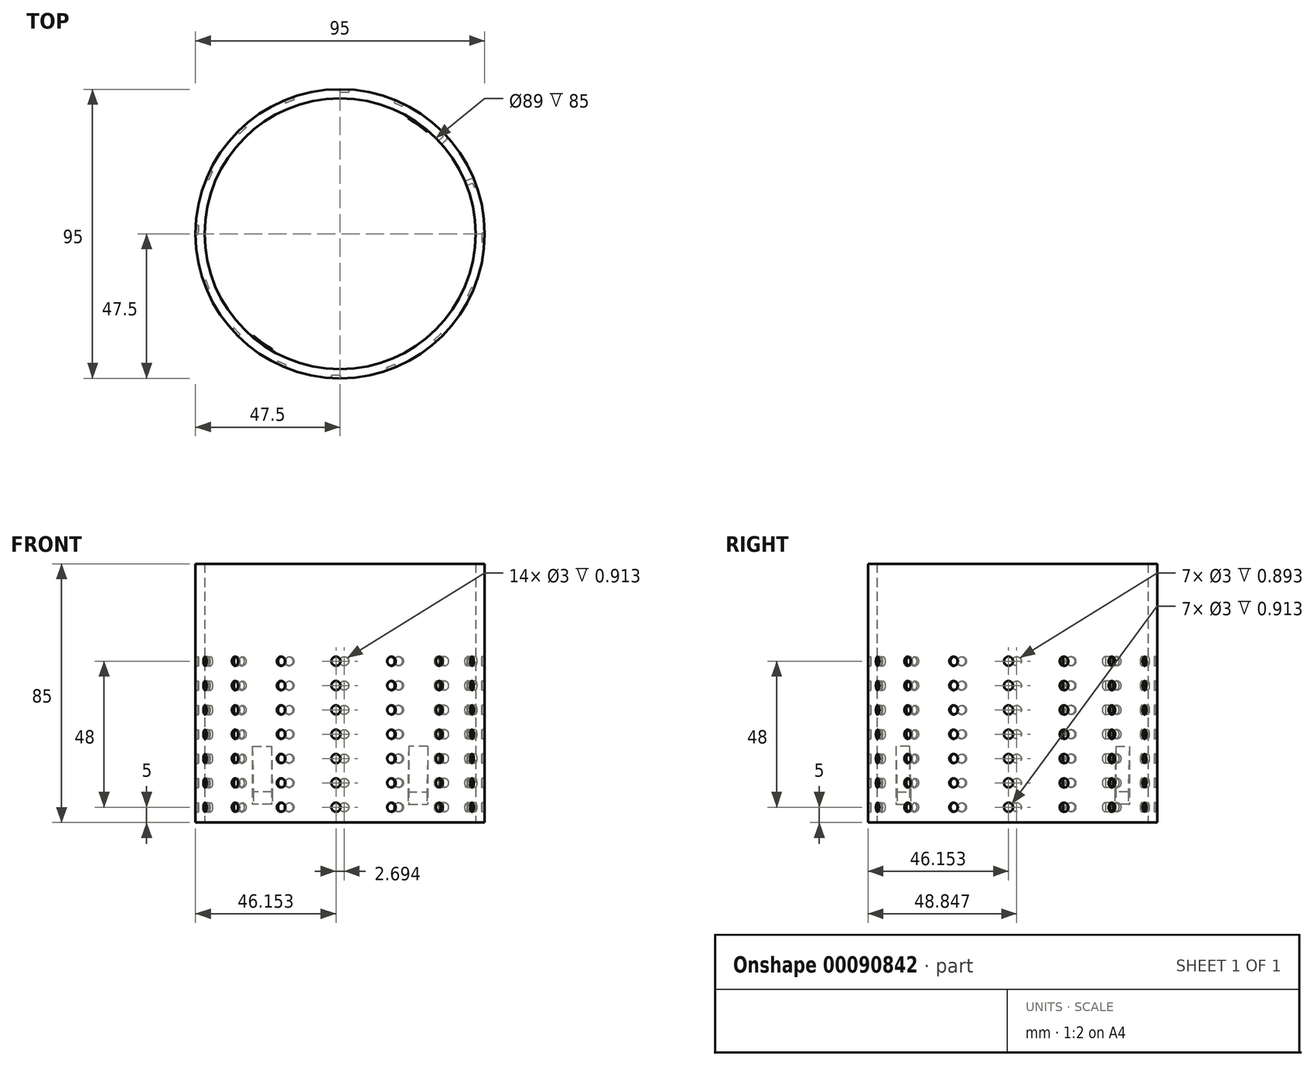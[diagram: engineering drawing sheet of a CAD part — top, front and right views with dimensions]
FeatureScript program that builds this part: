
annotation { "Feature Type Name" : "Feature", "Feature Type Description" : "" }
export const myFeature = defineFeature(function(context is Context, id is Id, definition is map)
    precondition{}
    {
        {
            var Q0;
            Q0=qCreatedBy(makeId("Top.planeOp"),FACE);
            var sketch = newSketch(context, id + "F0", { "sketchPlane" : qUnion([Q0])});
            skCircle(sketch, "E0", {"center": v(0, 0) * mm, "radius": 44.5 * mm});
            skCircle(sketch, "E1", {"center": v(0, 0) * mm, "radius": 47.5 * mm});
            skCircle(sketch, "E2.cCircle", {"center": v(0, 0) * mm, "radius": 47.5 * mm, "construction": true});
            skLineSegment(sketch, "E2.0", {"start": v(-27.5, -38.72) * mm, "end": v(-40.23, -25.25) * mm});
            skLineSegment(sketch, "E2.1", {"start": v(-40.23, -25.25) * mm, "end": v(-46.83, -7.93) * mm});
            skLineSegment(sketch, "E2.2", {"start": v(-46.83, -7.93) * mm, "end": v(-46.3, 10.6) * mm});
            skLineSegment(sketch, "E2.3", {"start": v(-46.3, 10.6) * mm, "end": v(-38.72, 27.5) * mm});
            skLineSegment(sketch, "E2.4", {"start": v(-38.72, 27.5) * mm, "end": v(-25.25, 40.23) * mm});
            skLineSegment(sketch, "E2.5", {"start": v(-25.25, 40.23) * mm, "end": v(-7.93, 46.83) * mm});
            skLineSegment(sketch, "E2.6", {"start": v(-7.93, 46.83) * mm, "end": v(10.6, 46.3) * mm});
            skLineSegment(sketch, "E2.7", {"start": v(10.6, 46.3) * mm, "end": v(27.5, 38.72) * mm});
            skLineSegment(sketch, "E2.8", {"start": v(27.5, 38.72) * mm, "end": v(40.23, 25.25) * mm});
            skLineSegment(sketch, "E2.9", {"start": v(40.23, 25.25) * mm, "end": v(46.83, 7.93) * mm});
            skLineSegment(sketch, "E2.10", {"start": v(46.83, 7.93) * mm, "end": v(46.3, -10.6) * mm});
            skLineSegment(sketch, "E2.11", {"start": v(46.3, -10.6) * mm, "end": v(38.72, -27.5) * mm});
            skLineSegment(sketch, "E2.12", {"start": v(38.72, -27.5) * mm, "end": v(25.25, -40.23) * mm});
            skLineSegment(sketch, "E2.13", {"start": v(25.25, -40.23) * mm, "end": v(7.93, -46.83) * mm});
            skLineSegment(sketch, "E2.14", {"start": v(7.93, -46.83) * mm, "end": v(-10.6, -46.3) * mm});
            skLineSegment(sketch, "E2.15", {"start": v(-10.6, -46.3) * mm, "end": v(-27.5, -38.72) * mm});
            skLineSegment(sketch, "E3", {"start": v(-33.87, -31.99) * mm, "end": v(33.87, 31.99) * mm});
            skLineSegment(sketch, "E4", {"start": v(31.99, -33.87) * mm, "end": v(-32.61, 34.54) * mm});
            skLineSegment(sketch, "E5", {"start": v(-42.51, 19.05) * mm, "end": v(42.51, -19.05) * mm});
            skLineSegment(sketch, "E6", {"start": v(-46.57, 1.33) * mm, "end": v(46.57, -1.33) * mm});
            skLineSegment(sketch, "E7", {"start": v(-19.05, -42.51) * mm, "end": v(19.05, 42.51) * mm});
            skLineSegment(sketch, "E8", {"start": v(-43.53, -16.59) * mm, "end": v(43.53, 16.59) * mm});
            skLineSegment(sketch, "E9", {"start": v(-1.33, -46.57) * mm, "end": v(1.33, 46.57) * mm});
            skLineSegment(sketch, "E10", {"start": v(-16.59, 43.53) * mm, "end": v(16.59, -43.53) * mm});
            skSolve(sketch);
        }
        {
            var Q0;
            Q0 = qSketchRegion(id + "F0", true);
            extrude(context, id + "F1", {"entities" : qUnion([Q0]), "depth" : 85 * mm});
        }
        {
            var Q0;
            {var subQ3=sQuery(id+"F0.wireOp",EDGE,"E9");var subQ5=sQuery(id+"F0.wireOp",EDGE,"E0");var subQ6=makeQuery(id+"F0.imprint","INTERSECT",VERTEX,{"disambiguationData":[OD(1.0)],"derivedFrom":[subQ5,subQ3]});Q0=makeQuery(id+"F0.imprint","IMPRINT",FACE,{"disambiguationData":[TD([[makeQuery(id+"F0.imprint","IMPRINT",EDGE,{"disambiguationData":[TD([[subQ6,-1.0]])],"derivedFrom":subQ5}),-1.0]])]});}
            var Q1;
            {var subQ3=sQuery(id+"F0.wireOp",EDGE,"E0");var subQ7=sQuery(id+"F0.wireOp",EDGE,"E10");var subQ9=makeQuery(id+"F0.imprint","INTERSECT",VERTEX,{"disambiguationData":[OD(1.0)],"derivedFrom":[subQ3,subQ7]});Q1=makeQuery(id+"F0.imprint","IMPRINT",FACE,{"disambiguationData":[TD([[makeQuery(id+"F0.imprint","IMPRINT",EDGE,{"disambiguationData":[TD([[subQ9,-1.0]])],"derivedFrom":subQ3}),-1.0]])]});}
            var Q2;
            {var subQ0=sQuery(id+"F0.wireOp",EDGE,"E4");var subQ3=sQuery(id+"F0.wireOp",EDGE,"E0");var subQ4=makeQuery(id+"F0.imprint","INTERSECT",VERTEX,{"disambiguationData":[OD(1.0)],"derivedFrom":[subQ3,subQ0]});Q2=makeQuery(id+"F0.imprint","IMPRINT",FACE,{"disambiguationData":[TD([[makeQuery(id+"F0.imprint","IMPRINT",EDGE,{"disambiguationData":[TD([[subQ4,-1.0]])],"derivedFrom":subQ3}),-1.0]])]});}
            var Q3;
            {var subQ0=sQuery(id+"F0.wireOp",EDGE,"E5");var subQ3=sQuery(id+"F0.wireOp",EDGE,"E0");var subQ4=makeQuery(id+"F0.imprint","INTERSECT",VERTEX,{"disambiguationData":[OD(1.0)],"derivedFrom":[subQ3,subQ0]});Q3=makeQuery(id+"F0.imprint","IMPRINT",FACE,{"disambiguationData":[TD([[makeQuery(id+"F0.imprint","IMPRINT",EDGE,{"disambiguationData":[TD([[subQ4,-1.0]])],"derivedFrom":subQ3}),-1.0]])]});}
            var Q4;
            {var subQ5=sQuery(id+"F0.wireOp",EDGE,"E8");var subQ7=sQuery(id+"F0.wireOp",EDGE,"E0");var subQ9=makeQuery(id+"F0.imprint","INTERSECT",VERTEX,{"disambiguationData":[OD(0.0)],"derivedFrom":[subQ7,subQ5]});Q4=makeQuery(id+"F0.imprint","IMPRINT",FACE,{"disambiguationData":[TD([[makeQuery(id+"F0.imprint","IMPRINT",EDGE,{"disambiguationData":[TD([[subQ9,1.0]])],"derivedFrom":subQ7}),-1.0]])]});}
            var Q5;
            {var subQ5=sQuery(id+"F0.wireOp",EDGE,"E3");var subQ6=sQuery(id+"F0.wireOp",EDGE,"E0");var subQ7=makeQuery(id+"F0.imprint","INTERSECT",VERTEX,{"disambiguationData":[OD(0.0)],"derivedFrom":[subQ6,subQ5]});Q5=makeQuery(id+"F0.imprint","IMPRINT",FACE,{"disambiguationData":[TD([[makeQuery(id+"F0.imprint","IMPRINT",EDGE,{"disambiguationData":[TD([[subQ7,1.0]])],"derivedFrom":subQ6}),-1.0]])]});}
            var Q6;
            {var subQ3=sQuery(id+"F0.wireOp",EDGE,"E3");var subQ5=sQuery(id+"F0.wireOp",EDGE,"E0");var subQ6=makeQuery(id+"F0.imprint","INTERSECT",VERTEX,{"disambiguationData":[OD(0.0)],"derivedFrom":[subQ5,subQ3]});Q6=makeQuery(id+"F0.imprint","IMPRINT",FACE,{"disambiguationData":[TD([[makeQuery(id+"F0.imprint","IMPRINT",EDGE,{"disambiguationData":[TD([[subQ6,-1.0]])],"derivedFrom":subQ5}),-1.0]])]});}
            var Q7;
            {var subQ3=sQuery(id+"F0.wireOp",EDGE,"E7");var subQ5=sQuery(id+"F0.wireOp",EDGE,"E0");var subQ6=makeQuery(id+"F0.imprint","INTERSECT",VERTEX,{"disambiguationData":[OD(0.0)],"derivedFrom":[subQ5,subQ3]});Q7=makeQuery(id+"F0.imprint","IMPRINT",FACE,{"disambiguationData":[TD([[makeQuery(id+"F0.imprint","IMPRINT",EDGE,{"disambiguationData":[TD([[subQ6,-1.0]])],"derivedFrom":subQ5}),-1.0]])]});}
            var Q8;
            {var subQ0=sQuery(id+"F0.wireOp",EDGE,"E9");var subQ3=sQuery(id+"F0.wireOp",EDGE,"E0");var subQ4=makeQuery(id+"F0.imprint","INTERSECT",VERTEX,{"disambiguationData":[OD(0.0)],"derivedFrom":[subQ3,subQ0]});Q8=makeQuery(id+"F0.imprint","IMPRINT",FACE,{"disambiguationData":[TD([[makeQuery(id+"F0.imprint","IMPRINT",EDGE,{"disambiguationData":[TD([[subQ4,-1.0]])],"derivedFrom":subQ3}),-1.0]])]});}
            var Q9;
            {var subQ1=sQuery(id+"F0.wireOp",EDGE,"E0");var subQ7=sQuery(id+"F0.wireOp",EDGE,"E10");var subQ9=makeQuery(id+"F0.imprint","INTERSECT",VERTEX,{"disambiguationData":[OD(0.0)],"derivedFrom":[subQ1,subQ7]});Q9=makeQuery(id+"F0.imprint","IMPRINT",FACE,{"disambiguationData":[TD([[makeQuery(id+"F0.imprint","IMPRINT",EDGE,{"disambiguationData":[TD([[subQ9,-1.0]])],"derivedFrom":subQ1}),-1.0]])]});}
            var Q10;
            {var subQ0=sQuery(id+"F0.wireOp",EDGE,"E4");var subQ1=sQuery(id+"F0.wireOp",EDGE,"E0");var subQ2=makeQuery(id+"F0.imprint","INTERSECT",VERTEX,{"disambiguationData":[OD(0.0)],"derivedFrom":[subQ1,subQ0]});Q10=makeQuery(id+"F0.imprint","IMPRINT",FACE,{"disambiguationData":[TD([[makeQuery(id+"F0.imprint","IMPRINT",EDGE,{"disambiguationData":[TD([[subQ2,-1.0]])],"derivedFrom":subQ1}),-1.0]])]});}
            var Q11;
            {var subQ0=sQuery(id+"F0.wireOp",EDGE,"E5");var subQ3=sQuery(id+"F0.wireOp",EDGE,"E0");var subQ4=makeQuery(id+"F0.imprint","INTERSECT",VERTEX,{"disambiguationData":[OD(0.0)],"derivedFrom":[subQ3,subQ0]});Q11=makeQuery(id+"F0.imprint","IMPRINT",FACE,{"disambiguationData":[TD([[makeQuery(id+"F0.imprint","IMPRINT",EDGE,{"disambiguationData":[TD([[subQ4,-1.0]])],"derivedFrom":subQ3}),-1.0]])]});}
            var Q12;
            {var subQ0=sQuery(id+"F0.wireOp",EDGE,"E6");var subQ3=sQuery(id+"F0.wireOp",EDGE,"E0");var subQ4=makeQuery(id+"F0.imprint","INTERSECT",VERTEX,{"disambiguationData":[OD(0.0)],"derivedFrom":[subQ3,subQ0]});Q12=makeQuery(id+"F0.imprint","IMPRINT",FACE,{"disambiguationData":[TD([[makeQuery(id+"F0.imprint","IMPRINT",EDGE,{"disambiguationData":[TD([[subQ4,-1.0]])],"derivedFrom":subQ3}),-1.0]])]});}
            var Q13;
            {var subQ3=sQuery(id+"F0.wireOp",EDGE,"E0");var subQ7=sQuery(id+"F0.wireOp",EDGE,"E8");var subQ9=makeQuery(id+"F0.imprint","INTERSECT",VERTEX,{"disambiguationData":[OD(1.0)],"derivedFrom":[subQ3,subQ7]});Q13=makeQuery(id+"F0.imprint","IMPRINT",FACE,{"disambiguationData":[TD([[makeQuery(id+"F0.imprint","IMPRINT",EDGE,{"disambiguationData":[TD([[subQ9,-1.0]])],"derivedFrom":subQ3}),-1.0]])]});}
            var Q14;
            {var subQ0=sQuery(id+"F0.wireOp",EDGE,"E3");var subQ3=sQuery(id+"F0.wireOp",EDGE,"E0");var subQ4=makeQuery(id+"F0.imprint","INTERSECT",VERTEX,{"disambiguationData":[OD(1.0)],"derivedFrom":[subQ3,subQ0]});Q14=makeQuery(id+"F0.imprint","IMPRINT",FACE,{"disambiguationData":[TD([[makeQuery(id+"F0.imprint","IMPRINT",EDGE,{"disambiguationData":[TD([[subQ4,-1.0]])],"derivedFrom":subQ3}),-1.0]])]});}
            var Q15;
            {var subQ0=sQuery(id+"F0.wireOp",EDGE,"E7");var subQ3=sQuery(id+"F0.wireOp",EDGE,"E0");var subQ4=makeQuery(id+"F0.imprint","INTERSECT",VERTEX,{"disambiguationData":[OD(1.0)],"derivedFrom":[subQ3,subQ0]});Q15=makeQuery(id+"F0.imprint","IMPRINT",FACE,{"disambiguationData":[TD([[makeQuery(id+"F0.imprint","IMPRINT",EDGE,{"disambiguationData":[TD([[subQ4,-1.0]])],"derivedFrom":subQ3}),-1.0]])]});}
            extrude(context, id + "F2", {"entities" : qUnion([Q0, Q1, Q2, Q3, Q4, Q5, Q6, Q7, Q8, Q9, Q10, Q11, Q12, Q13, Q14, Q15]), "depth" : 85 * mm});
        }
        {
            var Q0;
            Q0=makeQuery(id+"F2.opExtrude","SWEPT_FACE",FACE,{"disambiguationData":[OSD([sQuery(id+"F0.wireOp",EDGE,"E2.13")])]});
            var sketch = newSketch(context, id + "F3", { "sketchPlane" : qUnion([Q0])});
            skLineSegment(sketch, "E11", {"start": v(0, 85) * mm, "end": v(0, 0) * mm});
            skCircle(sketch, "E12", {"center": v(0, 5) * mm, "radius": 1.5 * mm});
            skCircle(sketch, "E13", {"center": v(0, 13) * mm, "radius": 1.5 * mm});
            skCircle(sketch, "E14", {"center": v(0, 21) * mm, "radius": 1.5 * mm});
            skCircle(sketch, "E15", {"center": v(0, 29) * mm, "radius": 1.5 * mm});
            skCircle(sketch, "E16", {"center": v(0, 37) * mm, "radius": 1.5 * mm});
            skCircle(sketch, "E17", {"center": v(0, 45) * mm, "radius": 1.5 * mm});
            skCircle(sketch, "E18", {"center": v(0, 53) * mm, "radius": 1.5 * mm});
            skSolve(sketch);
        }
        {
            var Q0;
            Q0=makeQuery(id+"F2.opExtrude","SWEPT_FACE",FACE,{"disambiguationData":[OSD([sQuery(id+"F0.wireOp",EDGE,"E2.12")])]});
            var sketch = newSketch(context, id + "F4", { "sketchPlane" : qUnion([Q0])});
            skLineSegment(sketch, "E19", {"start": v(0, 85) * mm, "end": v(0, 0) * mm});
            skCircle(sketch, "E20", {"center": v(0, 5) * mm, "radius": 1.5 * mm});
            skCircle(sketch, "E21", {"center": v(0, 13) * mm, "radius": 1.5 * mm});
            skCircle(sketch, "E22", {"center": v(0, 21) * mm, "radius": 1.5 * mm});
            skCircle(sketch, "E23", {"center": v(0, 29) * mm, "radius": 1.5 * mm});
            skCircle(sketch, "E24", {"center": v(0, 37) * mm, "radius": 1.5 * mm});
            skCircle(sketch, "E25", {"center": v(0, 45) * mm, "radius": 1.5 * mm});
            skCircle(sketch, "E26", {"center": v(0, 53) * mm, "radius": 1.5 * mm});
            skSolve(sketch);
        }
        {
            var Q0;
            Q0=makeQuery(id+"F2.opExtrude","SWEPT_FACE",FACE,{"disambiguationData":[OSD([sQuery(id+"F0.wireOp",EDGE,"E2.11")])]});
            var sketch = newSketch(context, id + "F5", { "sketchPlane" : qUnion([Q0])});
            skLineSegment(sketch, "E27", {"start": v(0, 85) * mm, "end": v(0, 0) * mm});
            skCircle(sketch, "E28", {"center": v(0, 5) * mm, "radius": 1.5 * mm});
            skCircle(sketch, "E29", {"center": v(0, 13) * mm, "radius": 1.5 * mm});
            skCircle(sketch, "E30", {"center": v(0, 21) * mm, "radius": 1.5 * mm});
            skCircle(sketch, "E31", {"center": v(0, 29) * mm, "radius": 1.5 * mm});
            skCircle(sketch, "E32", {"center": v(0, 37) * mm, "radius": 1.5 * mm});
            skCircle(sketch, "E33", {"center": v(0, 45) * mm, "radius": 1.5 * mm});
            skCircle(sketch, "E34", {"center": v(0, 53) * mm, "radius": 1.5 * mm});
            skSolve(sketch);
        }
        {
            var Q0;
            Q0=makeQuery(id+"F2.opExtrude","SWEPT_FACE",FACE,{"disambiguationData":[OSD([sQuery(id+"F0.wireOp",EDGE,"E2.10")])]});
            var sketch = newSketch(context, id + "F6", { "sketchPlane" : qUnion([Q0])});
            skLineSegment(sketch, "E35", {"start": v(0, 85) * mm, "end": v(0, 0) * mm});
            skCircle(sketch, "E36", {"center": v(0, 5) * mm, "radius": 1.5 * mm});
            skCircle(sketch, "E37", {"center": v(0, 13) * mm, "radius": 1.5 * mm});
            skCircle(sketch, "E38", {"center": v(0, 21) * mm, "radius": 1.5 * mm});
            skCircle(sketch, "E39", {"center": v(0, 29) * mm, "radius": 1.5 * mm});
            skCircle(sketch, "E40", {"center": v(0, 37) * mm, "radius": 1.5 * mm});
            skCircle(sketch, "E41", {"center": v(0, 45) * mm, "radius": 1.5 * mm});
            skCircle(sketch, "E42", {"center": v(0, 53) * mm, "radius": 1.5 * mm});
            skSolve(sketch);
        }
        {
            var Q0;
            Q0=makeQuery(id+"F2.opExtrude","SWEPT_FACE",FACE,{"disambiguationData":[OSD([sQuery(id+"F0.wireOp",EDGE,"E2.9")])]});
            var sketch = newSketch(context, id + "F7", { "sketchPlane" : qUnion([Q0])});
            skLineSegment(sketch, "E43", {"start": v(0, 85) * mm, "end": v(0, 0) * mm});
            skCircle(sketch, "E44", {"center": v(0, 5) * mm, "radius": 1.5 * mm});
            skCircle(sketch, "E45", {"center": v(0, 13) * mm, "radius": 1.5 * mm});
            skCircle(sketch, "E46", {"center": v(0, 21) * mm, "radius": 1.5 * mm});
            skCircle(sketch, "E47", {"center": v(0, 29) * mm, "radius": 1.5 * mm});
            skCircle(sketch, "E48", {"center": v(0, 37) * mm, "radius": 1.5 * mm});
            skCircle(sketch, "E49", {"center": v(0, 45) * mm, "radius": 1.5 * mm});
            skCircle(sketch, "E50", {"center": v(0, 53) * mm, "radius": 1.5 * mm});
            skSolve(sketch);
        }
        {
            var Q0;
            Q0=makeQuery(id+"F2.opExtrude","SWEPT_FACE",FACE,{"disambiguationData":[OSD([sQuery(id+"F0.wireOp",EDGE,"E2.8")])]});
            var sketch = newSketch(context, id + "F8", { "sketchPlane" : qUnion([Q0])});
            skLineSegment(sketch, "E51", {"start": v(0, 85) * mm, "end": v(0, 0) * mm});
            skCircle(sketch, "E52", {"center": v(0, 5) * mm, "radius": 1.5 * mm});
            skCircle(sketch, "E53", {"center": v(0, 13) * mm, "radius": 1.5 * mm});
            skCircle(sketch, "E54", {"center": v(0, 21) * mm, "radius": 1.5 * mm});
            skCircle(sketch, "E55", {"center": v(0, 29) * mm, "radius": 1.5 * mm});
            skCircle(sketch, "E56", {"center": v(0, 37) * mm, "radius": 1.5 * mm});
            skCircle(sketch, "E57", {"center": v(0, 45) * mm, "radius": 1.5 * mm});
            skCircle(sketch, "E58", {"center": v(0, 53) * mm, "radius": 1.5 * mm});
            skSolve(sketch);
        }
        {
            var Q0;
            Q0=makeQuery(id+"F2.opExtrude","SWEPT_FACE",FACE,{"disambiguationData":[OSD([sQuery(id+"F0.wireOp",EDGE,"E2.7")])]});
            var sketch = newSketch(context, id + "F9", { "sketchPlane" : qUnion([Q0])});
            skLineSegment(sketch, "E59", {"start": v(0, 85) * mm, "end": v(0, 0) * mm});
            skCircle(sketch, "E60", {"center": v(0, 5) * mm, "radius": 1.5 * mm});
            skCircle(sketch, "E61", {"center": v(0, 13) * mm, "radius": 1.5 * mm});
            skCircle(sketch, "E62", {"center": v(0, 21) * mm, "radius": 1.5 * mm});
            skCircle(sketch, "E63", {"center": v(0, 29) * mm, "radius": 1.5 * mm});
            skCircle(sketch, "E64", {"center": v(0, 37) * mm, "radius": 1.5 * mm});
            skCircle(sketch, "E65", {"center": v(0, 45) * mm, "radius": 1.5 * mm});
            skCircle(sketch, "E66", {"center": v(0, 53) * mm, "radius": 1.5 * mm});
            skSolve(sketch);
        }
        {
            var Q0;
            Q0=makeQuery(id+"F2.opExtrude","SWEPT_FACE",FACE,{"disambiguationData":[OSD([sQuery(id+"F0.wireOp",EDGE,"E2.6")])]});
            var sketch = newSketch(context, id + "F10", { "sketchPlane" : qUnion([Q0])});
            skLineSegment(sketch, "E67", {"start": v(0, 85) * mm, "end": v(0, 0) * mm});
            skCircle(sketch, "E68", {"center": v(0, 5) * mm, "radius": 1.5 * mm});
            skCircle(sketch, "E69", {"center": v(0, 13) * mm, "radius": 1.5 * mm});
            skCircle(sketch, "E70", {"center": v(0, 21) * mm, "radius": 1.5 * mm});
            skCircle(sketch, "E71", {"center": v(0, 29) * mm, "radius": 1.5 * mm});
            skCircle(sketch, "E72", {"center": v(0, 37) * mm, "radius": 1.5 * mm});
            skCircle(sketch, "E73", {"center": v(0, 45) * mm, "radius": 1.5 * mm});
            skCircle(sketch, "E74", {"center": v(0, 53) * mm, "radius": 1.5 * mm});
            skSolve(sketch);
        }
        {
            var Q0;
            Q0=makeQuery(id+"F2.opExtrude","SWEPT_FACE",FACE,{"disambiguationData":[OSD([sQuery(id+"F0.wireOp",EDGE,"E2.5")])]});
            var sketch = newSketch(context, id + "F11", { "sketchPlane" : qUnion([Q0])});
            skLineSegment(sketch, "E75", {"start": v(0, 85) * mm, "end": v(0, 0) * mm});
            skCircle(sketch, "E76", {"center": v(0, 5) * mm, "radius": 1.5 * mm});
            skCircle(sketch, "E77", {"center": v(0, 13) * mm, "radius": 1.5 * mm});
            skCircle(sketch, "E78", {"center": v(0, 21) * mm, "radius": 1.5 * mm});
            skCircle(sketch, "E79", {"center": v(0, 29) * mm, "radius": 1.5 * mm});
            skCircle(sketch, "E80", {"center": v(0, 37) * mm, "radius": 1.5 * mm});
            skCircle(sketch, "E81", {"center": v(0, 45) * mm, "radius": 1.5 * mm});
            skCircle(sketch, "E82", {"center": v(0, 53) * mm, "radius": 1.5 * mm});
            skSolve(sketch);
        }
        {
            var Q0;
            Q0=makeQuery(id+"F2.opExtrude","SWEPT_FACE",FACE,{"disambiguationData":[OSD([sQuery(id+"F0.wireOp",EDGE,"E2.4")])]});
            var sketch = newSketch(context, id + "F12", { "sketchPlane" : qUnion([Q0])});
            skLineSegment(sketch, "E83", {"start": v(0, 85) * mm, "end": v(0, 0) * mm});
            skCircle(sketch, "E84", {"center": v(0, 5) * mm, "radius": 1.5 * mm});
            skCircle(sketch, "E85", {"center": v(0, 13) * mm, "radius": 1.5 * mm});
            skCircle(sketch, "E86", {"center": v(0, 21) * mm, "radius": 1.5 * mm});
            skCircle(sketch, "E87", {"center": v(0, 29) * mm, "radius": 1.5 * mm});
            skCircle(sketch, "E88", {"center": v(0, 37) * mm, "radius": 1.5 * mm});
            skCircle(sketch, "E89", {"center": v(0, 45) * mm, "radius": 1.5 * mm});
            skCircle(sketch, "E90", {"center": v(0, 53) * mm, "radius": 1.5 * mm});
            skSolve(sketch);
        }
        {
            var Q0;
            Q0=makeQuery(id+"F2.opExtrude","SWEPT_FACE",FACE,{"disambiguationData":[OSD([sQuery(id+"F0.wireOp",EDGE,"E2.3")])]});
            var sketch = newSketch(context, id + "F13", { "sketchPlane" : qUnion([Q0])});
            skLineSegment(sketch, "E91", {"start": v(0, 85) * mm, "end": v(0, 0) * mm});
            skCircle(sketch, "E92", {"center": v(0, 5) * mm, "radius": 1.5 * mm});
            skCircle(sketch, "E93", {"center": v(0, 13) * mm, "radius": 1.5 * mm});
            skCircle(sketch, "E94", {"center": v(0, 21) * mm, "radius": 1.5 * mm});
            skCircle(sketch, "E95", {"center": v(0, 29) * mm, "radius": 1.5 * mm});
            skCircle(sketch, "E96", {"center": v(0, 37) * mm, "radius": 1.5 * mm});
            skCircle(sketch, "E97", {"center": v(0, 45) * mm, "radius": 1.5 * mm});
            skCircle(sketch, "E98", {"center": v(0, 53) * mm, "radius": 1.5 * mm});
            skSolve(sketch);
        }
        {
            var Q0;
            Q0=makeQuery(id+"F2.opExtrude","SWEPT_FACE",FACE,{"disambiguationData":[OSD([sQuery(id+"F0.wireOp",EDGE,"E2.2")])]});
            var sketch = newSketch(context, id + "F14", { "sketchPlane" : qUnion([Q0])});
            skLineSegment(sketch, "E99", {"start": v(0, 85) * mm, "end": v(0, 0) * mm});
            skCircle(sketch, "E100", {"center": v(0, 5) * mm, "radius": 1.5 * mm});
            skCircle(sketch, "E101", {"center": v(0, 13) * mm, "radius": 1.5 * mm});
            skCircle(sketch, "E102", {"center": v(0, 21) * mm, "radius": 1.5 * mm});
            skCircle(sketch, "E103", {"center": v(0, 29) * mm, "radius": 1.5 * mm});
            skCircle(sketch, "E104", {"center": v(0, 37) * mm, "radius": 1.5 * mm});
            skCircle(sketch, "E105", {"center": v(0, 45) * mm, "radius": 1.5 * mm});
            skCircle(sketch, "E106", {"center": v(0, 53) * mm, "radius": 1.5 * mm});
            skSolve(sketch);
        }
        {
            var Q0;
            Q0=makeQuery(id+"F2.opExtrude","SWEPT_FACE",FACE,{"disambiguationData":[OSD([sQuery(id+"F0.wireOp",EDGE,"E2.1")])]});
            var sketch = newSketch(context, id + "F15", { "sketchPlane" : qUnion([Q0])});
            skLineSegment(sketch, "E107", {"start": v(0, 85) * mm, "end": v(0, 0) * mm});
            skCircle(sketch, "E108", {"center": v(0, 5) * mm, "radius": 1.5 * mm});
            skCircle(sketch, "E109", {"center": v(0, 13) * mm, "radius": 1.5 * mm});
            skCircle(sketch, "E110", {"center": v(0, 21) * mm, "radius": 1.5 * mm});
            skCircle(sketch, "E111", {"center": v(0, 29) * mm, "radius": 1.5 * mm});
            skCircle(sketch, "E112", {"center": v(0, 37) * mm, "radius": 1.5 * mm});
            skCircle(sketch, "E113", {"center": v(0, 45) * mm, "radius": 1.5 * mm});
            skCircle(sketch, "E114", {"center": v(0, 53) * mm, "radius": 1.5 * mm});
            skSolve(sketch);
        }
        {
            var Q0;
            Q0=makeQuery(id+"F2.opExtrude","SWEPT_FACE",FACE,{"disambiguationData":[OSD([sQuery(id+"F0.wireOp",EDGE,"E2.0")])]});
            var sketch = newSketch(context, id + "F16", { "sketchPlane" : qUnion([Q0])});
            skLineSegment(sketch, "E115", {"start": v(0, 85) * mm, "end": v(0, 0) * mm});
            skCircle(sketch, "E116", {"center": v(0, 5) * mm, "radius": 1.5 * mm});
            skCircle(sketch, "E117", {"center": v(0, 13) * mm, "radius": 1.5 * mm});
            skCircle(sketch, "E118", {"center": v(0, 21) * mm, "radius": 1.5 * mm});
            skCircle(sketch, "E119", {"center": v(0, 29) * mm, "radius": 1.5 * mm});
            skCircle(sketch, "E120", {"center": v(0, 37) * mm, "radius": 1.5 * mm});
            skCircle(sketch, "E121", {"center": v(0, 45) * mm, "radius": 1.5 * mm});
            skCircle(sketch, "E122", {"center": v(0, 53) * mm, "radius": 1.5 * mm});
            skSolve(sketch);
        }
        {
            var Q0;
            Q0=makeQuery(id+"F2.opExtrude","SWEPT_FACE",FACE,{"disambiguationData":[OSD([sQuery(id+"F0.wireOp",EDGE,"E2.15")])]});
            var sketch = newSketch(context, id + "F17", { "sketchPlane" : qUnion([Q0])});
            skLineSegment(sketch, "E123", {"start": v(0, 85) * mm, "end": v(0, 0) * mm});
            skCircle(sketch, "E124", {"center": v(0, 5) * mm, "radius": 1.5 * mm});
            skCircle(sketch, "E125", {"center": v(0, 13) * mm, "radius": 1.5 * mm});
            skCircle(sketch, "E126", {"center": v(0, 21) * mm, "radius": 1.5 * mm});
            skCircle(sketch, "E127", {"center": v(0, 29) * mm, "radius": 1.5 * mm});
            skCircle(sketch, "E128", {"center": v(0, 37) * mm, "radius": 1.5 * mm});
            skCircle(sketch, "E129", {"center": v(0, 45) * mm, "radius": 1.5 * mm});
            skCircle(sketch, "E130", {"center": v(0, 53) * mm, "radius": 1.5 * mm});
            skSolve(sketch);
        }
        {
            var Q0;
            Q0=makeQuery(id+"F2.opExtrude","SWEPT_FACE",FACE,{"disambiguationData":[OSD([sQuery(id+"F0.wireOp",EDGE,"E2.14")])]});
            var sketch = newSketch(context, id + "F18", { "sketchPlane" : qUnion([Q0])});
            skLineSegment(sketch, "E131", {"start": v(0, 85) * mm, "end": v(0, 0) * mm});
            skCircle(sketch, "E132", {"center": v(0, 5) * mm, "radius": 1.5 * mm});
            skCircle(sketch, "E133", {"center": v(0, 13) * mm, "radius": 1.5 * mm});
            skCircle(sketch, "E134", {"center": v(0, 21) * mm, "radius": 1.5 * mm});
            skCircle(sketch, "E135", {"center": v(0, 29) * mm, "radius": 1.5 * mm});
            skCircle(sketch, "E136", {"center": v(0, 37) * mm, "radius": 1.5 * mm});
            skCircle(sketch, "E137", {"center": v(0, 45) * mm, "radius": 1.5 * mm});
            skCircle(sketch, "E138", {"center": v(0, 53) * mm, "radius": 1.5 * mm});
            skSolve(sketch);
        }
        {
            var Q0;
            Q0 = qSketchRegion(id + "F3", true);
            extrude(context, id + "F19", {"entities" : qUnion([Q0]), "endBound" : BoundingType.SYMMETRIC, "oppositeDirection" : true, "depth" : 25 * mm});
        }
        {
            var Q0;
            Q0 = qSketchRegion(id + "F4", true);
            extrude(context, id + "F20", {"entities" : qUnion([Q0]), "endBound" : BoundingType.SYMMETRIC, "depth" : 25 * mm});
        }
        {
            var Q0;
            Q0 = qSketchRegion(id + "F5", true);
            extrude(context, id + "F21", {"entities" : qUnion([Q0]), "endBound" : BoundingType.SYMMETRIC, "depth" : 25 * mm});
        }
        {
            var Q0;
            Q0 = qSketchRegion(id + "F6", true);
            extrude(context, id + "F22", {"entities" : qUnion([Q0]), "endBound" : BoundingType.SYMMETRIC, "depth" : 25 * mm});
        }
        {
            var Q0;
            Q0 = qSketchRegion(id + "F7", true);
            extrude(context, id + "F23", {"entities" : qUnion([Q0]), "endBound" : BoundingType.SYMMETRIC, "depth" : 25 * mm});
        }
        {
            var Q0;
            Q0 = qSketchRegion(id + "F8", true);
            extrude(context, id + "F24", {"entities" : qUnion([Q0]), "endBound" : BoundingType.SYMMETRIC, "depth" : 25 * mm});
        }
        {
            var Q0;
            Q0 = qSketchRegion(id + "F9", true);
            extrude(context, id + "F25", {"entities" : qUnion([Q0]), "endBound" : BoundingType.SYMMETRIC, "depth" : 25 * mm});
        }
        {
            var Q0;
            Q0 = qSketchRegion(id + "F10", true);
            extrude(context, id + "F26", {"entities" : qUnion([Q0]), "endBound" : BoundingType.SYMMETRIC, "depth" : 25 * mm});
        }
        {
            var Q0;
            Q0 = qSketchRegion(id + "F11", true);
            extrude(context, id + "F27", {"entities" : qUnion([Q0]), "endBound" : BoundingType.SYMMETRIC, "depth" : 25 * mm});
        }
        {
            var Q0;
            Q0 = qSketchRegion(id + "F12", true);
            extrude(context, id + "F28", {"entities" : qUnion([Q0]), "endBound" : BoundingType.SYMMETRIC, "depth" : 25 * mm});
        }
        {
            var Q0;
            Q0 = qSketchRegion(id + "F13", true);
            extrude(context, id + "F29", {"entities" : qUnion([Q0]), "endBound" : BoundingType.SYMMETRIC, "depth" : 25 * mm});
        }
        {
            var Q0;
            Q0 = qSketchRegion(id + "F14", true);
            extrude(context, id + "F30", {"entities" : qUnion([Q0]), "endBound" : BoundingType.SYMMETRIC, "depth" : 25 * mm});
        }
        {
            var Q0;
            Q0 = qSketchRegion(id + "F15", true);
            extrude(context, id + "F31", {"entities" : qUnion([Q0]), "endBound" : BoundingType.SYMMETRIC, "depth" : 25 * mm});
        }
        {
            var Q0;
            Q0 = qSketchRegion(id + "F16", true);
            extrude(context, id + "F32", {"entities" : qUnion([Q0]), "endBound" : BoundingType.SYMMETRIC, "depth" : 25 * mm});
        }
        {
            var Q0;
            Q0 = qSketchRegion(id + "F17", true);
            extrude(context, id + "F33", {"entities" : qUnion([Q0]), "endBound" : BoundingType.SYMMETRIC, "depth" : 25 * mm});
        }
        {
            var Q0;
            Q0 = qSketchRegion(id + "F18", true);
            extrude(context, id + "F34", {"entities" : qUnion([Q0]), "endBound" : BoundingType.SYMMETRIC, "depth" : 25 * mm});
        }
        {
            var Q0;
            Q0=makeQuery(id+"F31.opExtrude","SWEPT_BODY",BODY,{"disambiguationData":[OSD([sQuery(id+"F15.wireOp",EDGE,"E108")])]});
            var Q1;
            Q1=makeQuery(id+"F23.opExtrude","SWEPT_BODY",BODY,{"disambiguationData":[OSD([sQuery(id+"F7.wireOp",EDGE,"E44")])]});
            var Q2;
            Q2=makeQuery(id+"F23.opExtrude","SWEPT_BODY",BODY,{"disambiguationData":[OSD([sQuery(id+"F7.wireOp",EDGE,"E45")])]});
            var Q3;
            Q3=makeQuery(id+"F19.opExtrude","SWEPT_BODY",BODY,{"disambiguationData":[OSD([sQuery(id+"F3.wireOp",EDGE,"E12")])]});
            var Q4;
            Q4=makeQuery(id+"F19.opExtrude","SWEPT_BODY",BODY,{"disambiguationData":[OSD([sQuery(id+"F3.wireOp",EDGE,"E13")])]});
            var Q5;
            Q5=makeQuery(id+"F19.opExtrude","SWEPT_BODY",BODY,{"disambiguationData":[OSD([sQuery(id+"F3.wireOp",EDGE,"E14")])]});
            var Q6;
            Q6=makeQuery(id+"F19.opExtrude","SWEPT_BODY",BODY,{"disambiguationData":[OSD([sQuery(id+"F3.wireOp",EDGE,"E15")])]});
            var Q7;
            Q7=makeQuery(id+"F19.opExtrude","SWEPT_BODY",BODY,{"disambiguationData":[OSD([sQuery(id+"F3.wireOp",EDGE,"E16")])]});
            var Q8;
            Q8=makeQuery(id+"F19.opExtrude","SWEPT_BODY",BODY,{"disambiguationData":[OSD([sQuery(id+"F3.wireOp",EDGE,"E17")])]});
            var Q9;
            Q9=makeQuery(id+"F19.opExtrude","SWEPT_BODY",BODY,{"disambiguationData":[OSD([sQuery(id+"F3.wireOp",EDGE,"E18")])]});
            var Q10;
            Q10=makeQuery(id+"F20.opExtrude","SWEPT_BODY",BODY,{"disambiguationData":[OSD([sQuery(id+"F4.wireOp",EDGE,"E20")])]});
            var Q11;
            Q11=makeQuery(id+"F20.opExtrude","SWEPT_BODY",BODY,{"disambiguationData":[OSD([sQuery(id+"F4.wireOp",EDGE,"E21")])]});
            var Q12;
            Q12=makeQuery(id+"F20.opExtrude","SWEPT_BODY",BODY,{"disambiguationData":[OSD([sQuery(id+"F4.wireOp",EDGE,"E22")])]});
            var Q13;
            Q13=makeQuery(id+"F20.opExtrude","SWEPT_BODY",BODY,{"disambiguationData":[OSD([sQuery(id+"F4.wireOp",EDGE,"E23")])]});
            var Q14;
            Q14=makeQuery(id+"F20.opExtrude","SWEPT_BODY",BODY,{"disambiguationData":[OSD([sQuery(id+"F4.wireOp",EDGE,"E24")])]});
            var Q15;
            Q15=makeQuery(id+"F20.opExtrude","SWEPT_BODY",BODY,{"disambiguationData":[OSD([sQuery(id+"F4.wireOp",EDGE,"E25")])]});
            var Q16;
            Q16=makeQuery(id+"F20.opExtrude","SWEPT_BODY",BODY,{"disambiguationData":[OSD([sQuery(id+"F4.wireOp",EDGE,"E26")])]});
            var Q17;
            Q17=makeQuery(id+"F21.opExtrude","SWEPT_BODY",BODY,{"disambiguationData":[OSD([sQuery(id+"F5.wireOp",EDGE,"E28")])]});
            var Q18;
            Q18=makeQuery(id+"F21.opExtrude","SWEPT_BODY",BODY,{"disambiguationData":[OSD([sQuery(id+"F5.wireOp",EDGE,"E29")])]});
            var Q19;
            Q19=makeQuery(id+"F21.opExtrude","SWEPT_BODY",BODY,{"disambiguationData":[OSD([sQuery(id+"F5.wireOp",EDGE,"E30")])]});
            var Q20;
            Q20=makeQuery(id+"F21.opExtrude","SWEPT_BODY",BODY,{"disambiguationData":[OSD([sQuery(id+"F5.wireOp",EDGE,"E31")])]});
            var Q21;
            Q21=makeQuery(id+"F21.opExtrude","SWEPT_BODY",BODY,{"disambiguationData":[OSD([sQuery(id+"F5.wireOp",EDGE,"E32")])]});
            var Q22;
            Q22=makeQuery(id+"F21.opExtrude","SWEPT_BODY",BODY,{"disambiguationData":[OSD([sQuery(id+"F5.wireOp",EDGE,"E33")])]});
            var Q23;
            Q23=makeQuery(id+"F21.opExtrude","SWEPT_BODY",BODY,{"disambiguationData":[OSD([sQuery(id+"F5.wireOp",EDGE,"E34")])]});
            var Q24;
            Q24=makeQuery(id+"F22.opExtrude","SWEPT_BODY",BODY,{"disambiguationData":[OSD([sQuery(id+"F6.wireOp",EDGE,"E36")])]});
            var Q25;
            Q25=makeQuery(id+"F22.opExtrude","SWEPT_BODY",BODY,{"disambiguationData":[OSD([sQuery(id+"F6.wireOp",EDGE,"E37")])]});
            var Q26;
            Q26=makeQuery(id+"F22.opExtrude","SWEPT_BODY",BODY,{"disambiguationData":[OSD([sQuery(id+"F6.wireOp",EDGE,"E38")])]});
            var Q27;
            Q27=makeQuery(id+"F22.opExtrude","SWEPT_BODY",BODY,{"disambiguationData":[OSD([sQuery(id+"F6.wireOp",EDGE,"E39")])]});
            var Q28;
            Q28=makeQuery(id+"F22.opExtrude","SWEPT_BODY",BODY,{"disambiguationData":[OSD([sQuery(id+"F6.wireOp",EDGE,"E40")])]});
            var Q29;
            Q29=makeQuery(id+"F22.opExtrude","SWEPT_BODY",BODY,{"disambiguationData":[OSD([sQuery(id+"F6.wireOp",EDGE,"E41")])]});
            var Q30;
            Q30=makeQuery(id+"F22.opExtrude","SWEPT_BODY",BODY,{"disambiguationData":[OSD([sQuery(id+"F6.wireOp",EDGE,"E42")])]});
            var Q31;
            Q31=makeQuery(id+"F23.opExtrude","SWEPT_BODY",BODY,{"disambiguationData":[OSD([sQuery(id+"F7.wireOp",EDGE,"E46")])]});
            var Q32;
            Q32=makeQuery(id+"F23.opExtrude","SWEPT_BODY",BODY,{"disambiguationData":[OSD([sQuery(id+"F7.wireOp",EDGE,"E47")])]});
            var Q33;
            Q33=makeQuery(id+"F23.opExtrude","SWEPT_BODY",BODY,{"disambiguationData":[OSD([sQuery(id+"F7.wireOp",EDGE,"E48")])]});
            var Q34;
            Q34=makeQuery(id+"F23.opExtrude","SWEPT_BODY",BODY,{"disambiguationData":[OSD([sQuery(id+"F7.wireOp",EDGE,"E49")])]});
            var Q35;
            Q35=makeQuery(id+"F23.opExtrude","SWEPT_BODY",BODY,{"disambiguationData":[OSD([sQuery(id+"F7.wireOp",EDGE,"E50")])]});
            var Q36;
            Q36=makeQuery(id+"F27.opExtrude","SWEPT_BODY",BODY,{"disambiguationData":[OSD([sQuery(id+"F11.wireOp",EDGE,"E76")])]});
            var Q37;
            Q37=makeQuery(id+"F27.opExtrude","SWEPT_BODY",BODY,{"disambiguationData":[OSD([sQuery(id+"F11.wireOp",EDGE,"E77")])]});
            var Q38;
            Q38=makeQuery(id+"F24.opExtrude","SWEPT_BODY",BODY,{"disambiguationData":[OSD([sQuery(id+"F8.wireOp",EDGE,"E52")])]});
            var Q39;
            Q39=makeQuery(id+"F24.opExtrude","SWEPT_BODY",BODY,{"disambiguationData":[OSD([sQuery(id+"F8.wireOp",EDGE,"E53")])]});
            var Q40;
            Q40=makeQuery(id+"F24.opExtrude","SWEPT_BODY",BODY,{"disambiguationData":[OSD([sQuery(id+"F8.wireOp",EDGE,"E54")])]});
            var Q41;
            Q41=makeQuery(id+"F24.opExtrude","SWEPT_BODY",BODY,{"disambiguationData":[OSD([sQuery(id+"F8.wireOp",EDGE,"E55")])]});
            var Q42;
            Q42=makeQuery(id+"F24.opExtrude","SWEPT_BODY",BODY,{"disambiguationData":[OSD([sQuery(id+"F8.wireOp",EDGE,"E56")])]});
            var Q43;
            Q43=makeQuery(id+"F24.opExtrude","SWEPT_BODY",BODY,{"disambiguationData":[OSD([sQuery(id+"F8.wireOp",EDGE,"E57")])]});
            var Q44;
            Q44=makeQuery(id+"F24.opExtrude","SWEPT_BODY",BODY,{"disambiguationData":[OSD([sQuery(id+"F8.wireOp",EDGE,"E58")])]});
            var Q45;
            Q45=makeQuery(id+"F25.opExtrude","SWEPT_BODY",BODY,{"disambiguationData":[OSD([sQuery(id+"F9.wireOp",EDGE,"E60")])]});
            var Q46;
            Q46=makeQuery(id+"F25.opExtrude","SWEPT_BODY",BODY,{"disambiguationData":[OSD([sQuery(id+"F9.wireOp",EDGE,"E61")])]});
            var Q47;
            Q47=makeQuery(id+"F25.opExtrude","SWEPT_BODY",BODY,{"disambiguationData":[OSD([sQuery(id+"F9.wireOp",EDGE,"E62")])]});
            var Q48;
            Q48=makeQuery(id+"F25.opExtrude","SWEPT_BODY",BODY,{"disambiguationData":[OSD([sQuery(id+"F9.wireOp",EDGE,"E63")])]});
            var Q49;
            Q49=makeQuery(id+"F25.opExtrude","SWEPT_BODY",BODY,{"disambiguationData":[OSD([sQuery(id+"F9.wireOp",EDGE,"E64")])]});
            var Q50;
            Q50=makeQuery(id+"F25.opExtrude","SWEPT_BODY",BODY,{"disambiguationData":[OSD([sQuery(id+"F9.wireOp",EDGE,"E65")])]});
            var Q51;
            Q51=makeQuery(id+"F25.opExtrude","SWEPT_BODY",BODY,{"disambiguationData":[OSD([sQuery(id+"F9.wireOp",EDGE,"E66")])]});
            var Q52;
            Q52=makeQuery(id+"F26.opExtrude","SWEPT_BODY",BODY,{"disambiguationData":[OSD([sQuery(id+"F10.wireOp",EDGE,"E68")])]});
            var Q53;
            Q53=makeQuery(id+"F26.opExtrude","SWEPT_BODY",BODY,{"disambiguationData":[OSD([sQuery(id+"F10.wireOp",EDGE,"E69")])]});
            var Q54;
            Q54=makeQuery(id+"F26.opExtrude","SWEPT_BODY",BODY,{"disambiguationData":[OSD([sQuery(id+"F10.wireOp",EDGE,"E70")])]});
            var Q55;
            Q55=makeQuery(id+"F26.opExtrude","SWEPT_BODY",BODY,{"disambiguationData":[OSD([sQuery(id+"F10.wireOp",EDGE,"E71")])]});
            var Q56;
            Q56=makeQuery(id+"F26.opExtrude","SWEPT_BODY",BODY,{"disambiguationData":[OSD([sQuery(id+"F10.wireOp",EDGE,"E72")])]});
            var Q57;
            Q57=makeQuery(id+"F26.opExtrude","SWEPT_BODY",BODY,{"disambiguationData":[OSD([sQuery(id+"F10.wireOp",EDGE,"E73")])]});
            var Q58;
            Q58=makeQuery(id+"F26.opExtrude","SWEPT_BODY",BODY,{"disambiguationData":[OSD([sQuery(id+"F10.wireOp",EDGE,"E74")])]});
            var Q59;
            Q59=makeQuery(id+"F27.opExtrude","SWEPT_BODY",BODY,{"disambiguationData":[OSD([sQuery(id+"F11.wireOp",EDGE,"E78")])]});
            var Q60;
            Q60=makeQuery(id+"F27.opExtrude","SWEPT_BODY",BODY,{"disambiguationData":[OSD([sQuery(id+"F11.wireOp",EDGE,"E79")])]});
            var Q61;
            Q61=makeQuery(id+"F27.opExtrude","SWEPT_BODY",BODY,{"disambiguationData":[OSD([sQuery(id+"F11.wireOp",EDGE,"E80")])]});
            var Q62;
            Q62=makeQuery(id+"F27.opExtrude","SWEPT_BODY",BODY,{"disambiguationData":[OSD([sQuery(id+"F11.wireOp",EDGE,"E81")])]});
            var Q63;
            Q63=makeQuery(id+"F27.opExtrude","SWEPT_BODY",BODY,{"disambiguationData":[OSD([sQuery(id+"F11.wireOp",EDGE,"E82")])]});
            var Q64;
            Q64=makeQuery(id+"F28.opExtrude","SWEPT_BODY",BODY,{"disambiguationData":[OSD([sQuery(id+"F12.wireOp",EDGE,"E86")])]});
            var Q65;
            Q65=makeQuery(id+"F28.opExtrude","SWEPT_BODY",BODY,{"disambiguationData":[OSD([sQuery(id+"F12.wireOp",EDGE,"E87")])]});
            var Q66;
            Q66=makeQuery(id+"F28.opExtrude","SWEPT_BODY",BODY,{"disambiguationData":[OSD([sQuery(id+"F12.wireOp",EDGE,"E88")])]});
            var Q67;
            Q67=makeQuery(id+"F28.opExtrude","SWEPT_BODY",BODY,{"disambiguationData":[OSD([sQuery(id+"F12.wireOp",EDGE,"E89")])]});
            var Q68;
            Q68=makeQuery(id+"F28.opExtrude","SWEPT_BODY",BODY,{"disambiguationData":[OSD([sQuery(id+"F12.wireOp",EDGE,"E90")])]});
            var Q69;
            Q69=makeQuery(id+"F30.opExtrude","SWEPT_BODY",BODY,{"disambiguationData":[OSD([sQuery(id+"F14.wireOp",EDGE,"E100")])]});
            var Q70;
            Q70=makeQuery(id+"F29.opExtrude","SWEPT_BODY",BODY,{"disambiguationData":[OSD([sQuery(id+"F13.wireOp",EDGE,"E92")])]});
            var Q71;
            Q71=makeQuery(id+"F29.opExtrude","SWEPT_BODY",BODY,{"disambiguationData":[OSD([sQuery(id+"F13.wireOp",EDGE,"E93")])]});
            var Q72;
            Q72=makeQuery(id+"F29.opExtrude","SWEPT_BODY",BODY,{"disambiguationData":[OSD([sQuery(id+"F13.wireOp",EDGE,"E94")])]});
            var Q73;
            Q73=makeQuery(id+"F29.opExtrude","SWEPT_BODY",BODY,{"disambiguationData":[OSD([sQuery(id+"F13.wireOp",EDGE,"E95")])]});
            var Q74;
            Q74=makeQuery(id+"F29.opExtrude","SWEPT_BODY",BODY,{"disambiguationData":[OSD([sQuery(id+"F13.wireOp",EDGE,"E96")])]});
            var Q75;
            Q75=makeQuery(id+"F29.opExtrude","SWEPT_BODY",BODY,{"disambiguationData":[OSD([sQuery(id+"F13.wireOp",EDGE,"E97")])]});
            var Q76;
            Q76=makeQuery(id+"F29.opExtrude","SWEPT_BODY",BODY,{"disambiguationData":[OSD([sQuery(id+"F13.wireOp",EDGE,"E98")])]});
            var Q77;
            Q77=makeQuery(id+"F30.opExtrude","SWEPT_BODY",BODY,{"disambiguationData":[OSD([sQuery(id+"F14.wireOp",EDGE,"E101")])]});
            var Q78;
            Q78=makeQuery(id+"F30.opExtrude","SWEPT_BODY",BODY,{"disambiguationData":[OSD([sQuery(id+"F14.wireOp",EDGE,"E102")])]});
            var Q79;
            Q79=makeQuery(id+"F30.opExtrude","SWEPT_BODY",BODY,{"disambiguationData":[OSD([sQuery(id+"F14.wireOp",EDGE,"E103")])]});
            var Q80;
            Q80=makeQuery(id+"F30.opExtrude","SWEPT_BODY",BODY,{"disambiguationData":[OSD([sQuery(id+"F14.wireOp",EDGE,"E104")])]});
            var Q81;
            Q81=makeQuery(id+"F30.opExtrude","SWEPT_BODY",BODY,{"disambiguationData":[OSD([sQuery(id+"F14.wireOp",EDGE,"E105")])]});
            var Q82;
            Q82=makeQuery(id+"F30.opExtrude","SWEPT_BODY",BODY,{"disambiguationData":[OSD([sQuery(id+"F14.wireOp",EDGE,"E106")])]});
            var Q83;
            Q83=makeQuery(id+"F31.opExtrude","SWEPT_BODY",BODY,{"disambiguationData":[OSD([sQuery(id+"F15.wireOp",EDGE,"E109")])]});
            var Q84;
            Q84=makeQuery(id+"F31.opExtrude","SWEPT_BODY",BODY,{"disambiguationData":[OSD([sQuery(id+"F15.wireOp",EDGE,"E110")])]});
            var Q85;
            Q85=makeQuery(id+"F31.opExtrude","SWEPT_BODY",BODY,{"disambiguationData":[OSD([sQuery(id+"F15.wireOp",EDGE,"E111")])]});
            var Q86;
            Q86=makeQuery(id+"F31.opExtrude","SWEPT_BODY",BODY,{"disambiguationData":[OSD([sQuery(id+"F15.wireOp",EDGE,"E112")])]});
            var Q87;
            Q87=makeQuery(id+"F31.opExtrude","SWEPT_BODY",BODY,{"disambiguationData":[OSD([sQuery(id+"F15.wireOp",EDGE,"E113")])]});
            var Q88;
            Q88=makeQuery(id+"F31.opExtrude","SWEPT_BODY",BODY,{"disambiguationData":[OSD([sQuery(id+"F15.wireOp",EDGE,"E114")])]});
            var Q89;
            Q89=makeQuery(id+"F32.opExtrude","SWEPT_BODY",BODY,{"disambiguationData":[OSD([sQuery(id+"F16.wireOp",EDGE,"E116")])]});
            var Q90;
            Q90=makeQuery(id+"F32.opExtrude","SWEPT_BODY",BODY,{"disambiguationData":[OSD([sQuery(id+"F16.wireOp",EDGE,"E117")])]});
            var Q91;
            Q91=makeQuery(id+"F32.opExtrude","SWEPT_BODY",BODY,{"disambiguationData":[OSD([sQuery(id+"F16.wireOp",EDGE,"E118")])]});
            var Q92;
            Q92=makeQuery(id+"F32.opExtrude","SWEPT_BODY",BODY,{"disambiguationData":[OSD([sQuery(id+"F16.wireOp",EDGE,"E119")])]});
            var Q93;
            Q93=makeQuery(id+"F32.opExtrude","SWEPT_BODY",BODY,{"disambiguationData":[OSD([sQuery(id+"F16.wireOp",EDGE,"E120")])]});
            var Q94;
            Q94=makeQuery(id+"F32.opExtrude","SWEPT_BODY",BODY,{"disambiguationData":[OSD([sQuery(id+"F16.wireOp",EDGE,"E121")])]});
            var Q95;
            Q95=makeQuery(id+"F32.opExtrude","SWEPT_BODY",BODY,{"disambiguationData":[OSD([sQuery(id+"F16.wireOp",EDGE,"E122")])]});
            var Q96;
            Q96=makeQuery(id+"F33.opExtrude","SWEPT_BODY",BODY,{"disambiguationData":[OSD([sQuery(id+"F17.wireOp",EDGE,"E124")])]});
            var Q97;
            Q97=makeQuery(id+"F33.opExtrude","SWEPT_BODY",BODY,{"disambiguationData":[OSD([sQuery(id+"F17.wireOp",EDGE,"E125")])]});
            var Q98;
            Q98=makeQuery(id+"F33.opExtrude","SWEPT_BODY",BODY,{"disambiguationData":[OSD([sQuery(id+"F17.wireOp",EDGE,"E126")])]});
            var Q99;
            Q99=makeQuery(id+"F33.opExtrude","SWEPT_BODY",BODY,{"disambiguationData":[OSD([sQuery(id+"F17.wireOp",EDGE,"E127")])]});
            var Q100;
            Q100=makeQuery(id+"F33.opExtrude","SWEPT_BODY",BODY,{"disambiguationData":[OSD([sQuery(id+"F17.wireOp",EDGE,"E128")])]});
            var Q101;
            Q101=makeQuery(id+"F33.opExtrude","SWEPT_BODY",BODY,{"disambiguationData":[OSD([sQuery(id+"F17.wireOp",EDGE,"E129")])]});
            var Q102;
            Q102=makeQuery(id+"F33.opExtrude","SWEPT_BODY",BODY,{"disambiguationData":[OSD([sQuery(id+"F17.wireOp",EDGE,"E130")])]});
            var Q103;
            Q103=makeQuery(id+"F34.opExtrude","SWEPT_BODY",BODY,{"disambiguationData":[OSD([sQuery(id+"F18.wireOp",EDGE,"E132")])]});
            var Q104;
            Q104=makeQuery(id+"F34.opExtrude","SWEPT_BODY",BODY,{"disambiguationData":[OSD([sQuery(id+"F18.wireOp",EDGE,"E133")])]});
            var Q105;
            Q105=makeQuery(id+"F34.opExtrude","SWEPT_BODY",BODY,{"disambiguationData":[OSD([sQuery(id+"F18.wireOp",EDGE,"E134")])]});
            var Q106;
            Q106=makeQuery(id+"F34.opExtrude","SWEPT_BODY",BODY,{"disambiguationData":[OSD([sQuery(id+"F18.wireOp",EDGE,"E135")])]});
            var Q107;
            Q107=makeQuery(id+"F34.opExtrude","SWEPT_BODY",BODY,{"disambiguationData":[OSD([sQuery(id+"F18.wireOp",EDGE,"E136")])]});
            var Q108;
            Q108=makeQuery(id+"F34.opExtrude","SWEPT_BODY",BODY,{"disambiguationData":[OSD([sQuery(id+"F18.wireOp",EDGE,"E137")])]});
            var Q109;
            Q109=makeQuery(id+"F34.opExtrude","SWEPT_BODY",BODY,{"disambiguationData":[OSD([sQuery(id+"F18.wireOp",EDGE,"E138")])]});
            var Q110;
            Q110=makeQuery(id+"F28.opExtrude","SWEPT_BODY",BODY,{"disambiguationData":[OSD([sQuery(id+"F12.wireOp",EDGE,"E84")])]});
            var Q111;
            Q111=makeQuery(id+"F28.opExtrude","SWEPT_BODY",BODY,{"disambiguationData":[OSD([sQuery(id+"F12.wireOp",EDGE,"E85")])]});
            var Q112;
            Q112=makeQuery(id+"F1.opExtrude","SWEPT_BODY",BODY,{"disambiguationData":[OSD([sQuery(id+"F0.wireOp",EDGE,"E0"),sQuery(id+"F0.wireOp",EDGE,"E1")])]});
            booleanBodies(context, id + "F35", {"operationType" : BooleanOperationType.SUBTRACTION, "tools" : qUnion([Q0, Q1, Q2, Q3, Q4, Q5, Q6, Q7, Q8, Q9, Q10, Q11, Q12, Q13, Q14, Q15, Q16, Q17, Q18, Q19, Q20, Q21, Q22, Q23, Q24, Q25, Q26, Q27, Q28, Q29, Q30, Q31, Q32, Q33, Q34, Q35, Q36, Q37, Q38, Q39, Q40, Q41, Q42, Q43, Q44, Q45, Q46, Q47, Q48, Q49, Q50, Q51, Q52, Q53, Q54, Q55, Q56, Q57, Q58, Q59, Q60, Q61, Q62, Q63, Q64, Q65, Q66, Q67, Q68, Q69, Q70, Q71, Q72, Q73, Q74, Q75, Q76, Q77, Q78, Q79, Q80, Q81, Q82, Q83, Q84, Q85, Q86, Q87, Q88, Q89, Q90, Q91, Q92, Q93, Q94, Q95, Q96, Q97, Q98, Q99, Q100, Q101, Q102, Q103, Q104, Q105, Q106, Q107, Q108, Q109, Q110, Q111]), "targets" : qUnion([Q112])});
        }
        {
            var Q0;
            Q0=makeQuery(id+"F2.opExtrude","CAP_FACE",FACE,{"disambiguationData":[OSD([sQuery(id+"F0.wireOp",EDGE,"E0"),sQuery(id+"F0.wireOp",EDGE,"E2.0"),sQuery(id+"F0.wireOp",EDGE,"E2.1"),sQuery(id+"F0.wireOp",EDGE,"E2.2"),sQuery(id+"F0.wireOp",EDGE,"E2.3"),sQuery(id+"F0.wireOp",EDGE,"E2.4"),sQuery(id+"F0.wireOp",EDGE,"E2.5"),sQuery(id+"F0.wireOp",EDGE,"E2.6"),sQuery(id+"F0.wireOp",EDGE,"E2.7"),sQuery(id+"F0.wireOp",EDGE,"E2.8"),sQuery(id+"F0.wireOp",EDGE,"E2.9"),sQuery(id+"F0.wireOp",EDGE,"E2.10"),sQuery(id+"F0.wireOp",EDGE,"E2.11"),sQuery(id+"F0.wireOp",EDGE,"E2.12"),sQuery(id+"F0.wireOp",EDGE,"E2.13"),sQuery(id+"F0.wireOp",EDGE,"E2.14"),sQuery(id+"F0.wireOp",EDGE,"E2.15")])],"isStart":true});
            var sketch = newSketch(context, id + "F36", { "sketchPlane" : qUnion([Q0])});
            skCircle(sketch, "E139", {"center": v(0, 0) * mm, "radius": 44.5 * mm});
            skCircle(sketch, "E140", {"center": v(0, 0) * mm, "radius": 44 * mm});
            skLineSegment(sketch, "E141", {"start": v(-27.5, 38.72) * mm, "end": v(0, 0) * mm});
            skLineSegment(sketch, "E142", {"start": v(0, 0) * mm, "end": v(27.5, -38.72) * mm});
            skLineSegment(sketch, "E143", {"start": v(0, 0) * mm, "end": v(-30.37, 35.7) * mm});
            skLineSegment(sketch, "E144", {"start": v(0, 0) * mm, "end": v(-23.7, 40.43) * mm});
            skLineSegment(sketch, "E145", {"start": v(0, 0) * mm, "end": v(30.37, -35.7) * mm});
            skLineSegment(sketch, "E146", {"start": v(0, 0) * mm, "end": v(23.7, -40.43) * mm});
            skSolve(sketch);
        }
        {
            var Q0;
            {var subQ0=sQuery(id+"F36.wireOp",EDGE,"E142");var subQ1=sQuery(id+"F36.wireOp",EDGE,"E139");var subQ2=makeQuery(id+"F36.imprint","INTERSECT",VERTEX,{"derivedFrom":[subQ1,subQ0]});Q0=makeQuery(id+"F36.imprint","IMPRINT",FACE,{"disambiguationData":[TD([[makeQuery(id+"F36.imprint","IMPRINT",EDGE,{"disambiguationData":[TD([[subQ2,1.0]])],"derivedFrom":subQ1}),-1.0]])]});}
            var Q1;
            {var subQ0=sQuery(id+"F36.wireOp",EDGE,"E142");var subQ1=sQuery(id+"F36.wireOp",EDGE,"E139");var subQ2=makeQuery(id+"F36.imprint","INTERSECT",VERTEX,{"derivedFrom":[subQ1,subQ0]});Q1=makeQuery(id+"F36.imprint","IMPRINT",FACE,{"disambiguationData":[TD([[makeQuery(id+"F36.imprint","IMPRINT",EDGE,{"disambiguationData":[TD([[subQ2,-1.0]])],"derivedFrom":subQ1}),-1.0]])]});}
            var Q2;
            {var subQ0=sQuery(id+"F36.wireOp",EDGE,"E143");var subQ1=sQuery(id+"F36.wireOp",EDGE,"E139");var subQ2=makeQuery(id+"F36.imprint","INTERSECT",VERTEX,{"derivedFrom":[subQ1,subQ0]});Q2=makeQuery(id+"F36.imprint","IMPRINT",FACE,{"disambiguationData":[TD([[makeQuery(id+"F36.imprint","IMPRINT",EDGE,{"disambiguationData":[TD([[subQ2,-1.0]])],"derivedFrom":subQ1}),-1.0]])]});}
            var Q3;
            {var subQ0=sQuery(id+"F36.wireOp",EDGE,"E143");var subQ1=sQuery(id+"F36.wireOp",EDGE,"E139");var subQ2=makeQuery(id+"F36.imprint","INTERSECT",VERTEX,{"derivedFrom":[subQ1,subQ0]});Q3=makeQuery(id+"F36.imprint","IMPRINT",FACE,{"disambiguationData":[TD([[makeQuery(id+"F36.imprint","IMPRINT",EDGE,{"disambiguationData":[TD([[subQ2,-1.0]])],"derivedFrom":subQ1}),-1.0]])]});}
            var Q4;
            {var subQ0=sQuery(id+"F36.wireOp",EDGE,"E141");var subQ1=sQuery(id+"F36.wireOp",EDGE,"E139");var subQ2=makeQuery(id+"F36.imprint","INTERSECT",VERTEX,{"derivedFrom":[subQ1,subQ0]});Q4=makeQuery(id+"F36.imprint","IMPRINT",FACE,{"disambiguationData":[TD([[makeQuery(id+"F36.imprint","IMPRINT",EDGE,{"disambiguationData":[TD([[subQ2,-1.0]])],"derivedFrom":subQ1}),-1.0]])]});}
            extrude(context, id + "F37", {"entities" : qUnion([Q0, Q1, Q2, Q3, Q4]), "operationType" : NewBodyOperationType.ADD, "oppositeDirection" : true, "depth" : 25 * mm});
        }
        {
            var Q0;
            {var subQ0=sQuery(id+"F36.wireOp",EDGE,"E140");var subQ1=sQuery(id+"F36.wireOp",EDGE,"E139");Q0=makeQuery(id+"F37.boolean.opBoolean","MERGE",FACE,{"derivedFrom":[makeQuery(id+"F1.opExtrude","CAP_FACE",FACE,{"disambiguationData":[OSD([sQuery(id+"F0.wireOp",EDGE,"E0"),sQuery(id+"F0.wireOp",EDGE,"E1")])],"isStart":true}),makeQuery(id+"F37.opExtrude","CAP_FACE",FACE,{"disambiguationData":[OSD([subQ1,subQ0,sQuery(id+"F36.wireOp",EDGE,"E145"),sQuery(id+"F36.wireOp",EDGE,"E146")])],"isStart":true}),makeQuery(id+"F37.opExtrude","CAP_FACE",FACE,{"disambiguationData":[OSD([subQ1,subQ0,sQuery(id+"F36.wireOp",EDGE,"E143"),sQuery(id+"F36.wireOp",EDGE,"E144")])],"isStart":true})]});}
            var Q1;
            {var subQ0=sQuery(id+"F36.wireOp",EDGE,"E140");var subQ1=sQuery(id+"F36.wireOp",EDGE,"E139");Q1=makeQuery(id+"F37.boolean.opBoolean","MERGE",FACE,{"derivedFrom":[makeQuery(id+"F1.opExtrude","CAP_FACE",FACE,{"disambiguationData":[OSD([sQuery(id+"F0.wireOp",EDGE,"E0"),sQuery(id+"F0.wireOp",EDGE,"E1")])],"isStart":true}),makeQuery(id+"F37.opExtrude","CAP_FACE",FACE,{"disambiguationData":[OSD([subQ1,subQ0,sQuery(id+"F36.wireOp",EDGE,"E145"),sQuery(id+"F36.wireOp",EDGE,"E146")])],"isStart":true}),makeQuery(id+"F37.opExtrude","CAP_FACE",FACE,{"disambiguationData":[OSD([subQ1,subQ0,sQuery(id+"F36.wireOp",EDGE,"E143"),sQuery(id+"F36.wireOp",EDGE,"E144")])],"isStart":true})]});}
            var sketch = newSketch(context, id + "F38", { "sketchPlane" : qUnion([Q0, Q1])});
            skCircle(sketch, "E147", {"center": v(0, 0) * mm, "radius": 44.5 * mm});
            skSolve(sketch);
        }
        {
            var Q0;
            {var subQ1=sQuery(id+"F36.wireOp",EDGE,"E143");var subQ2=makeQuery(id+"F37.opExtrude","CAP_EDGE",EDGE,{"disambiguationData":[OSD([subQ1])],"isStart":true});Q0=makeQuery(id+"F38.imprint","IMPRINT",FACE,{"disambiguationData":[TD([[makeQuery(id+"F38.imprint","IMPRINT",EDGE,{"derivedFrom":subQ2}),-1.0]])]});}
            var Q1;
            {var subQ1=sQuery(id+"F36.wireOp",EDGE,"E143");var subQ2=makeQuery(id+"F37.opExtrude","CAP_EDGE",EDGE,{"disambiguationData":[OSD([subQ1])],"isStart":true});Q1=makeQuery(id+"F38.imprint","IMPRINT",FACE,{"disambiguationData":[TD([[makeQuery(id+"F38.imprint","IMPRINT",EDGE,{"derivedFrom":subQ2}),-1.0]])]});}
            var Q2;
            {var subQ1=sQuery(id+"F36.wireOp",EDGE,"E145");var subQ2=makeQuery(id+"F37.opExtrude","CAP_EDGE",EDGE,{"disambiguationData":[OSD([subQ1])],"isStart":true});Q2=makeQuery(id+"F38.imprint","IMPRINT",FACE,{"disambiguationData":[TD([[makeQuery(id+"F38.imprint","IMPRINT",EDGE,{"derivedFrom":subQ2}),-1.0]])]});}
            extrude(context, id + "F39", {"entities" : qUnion([Q0, Q1, Q2]), "operationType" : NewBodyOperationType.REMOVE, "oppositeDirection" : true, "depth" : 6 * mm});
        }
        {
            var Q0;
            {var subQ0=sQuery(id+"F36.wireOp",EDGE,"E140");var subQ1=makeQuery(id+"F36.imprint","INTERSECT",VERTEX,{"derivedFrom":[subQ0,sQuery(id+"F36.wireOp",EDGE,"E141")]});Q0=makeQuery(id+"F37.opExtrude","CAP_EDGE",EDGE,{"disambiguationData":[OSD([subQ0]),TDD([makeQuery(id+"F36.imprint","IMPRINT",EDGE,{"disambiguationData":[TD([[subQ1,1.0]])],"derivedFrom":subQ0}),makeQuery(id+"F36.imprint","IMPRINT",EDGE,{"disambiguationData":[TD([[subQ1,-1.0]])],"derivedFrom":subQ0})])],"isStart":false});}
            var Q1;
            {var subQ0=sQuery(id+"F36.wireOp",EDGE,"E140");var subQ1=makeQuery(id+"F36.imprint","INTERSECT",VERTEX,{"derivedFrom":[subQ0,sQuery(id+"F36.wireOp",EDGE,"E142")]});Q1=makeQuery(id+"F37.opExtrude","CAP_EDGE",EDGE,{"disambiguationData":[OSD([subQ0]),TDD([makeQuery(id+"F36.imprint","IMPRINT",EDGE,{"disambiguationData":[TD([[makeQuery(id+"F36.imprint","INTERSECT",VERTEX,{"derivedFrom":[subQ0,sQuery(id+"F36.wireOp",EDGE,"E146")]}),-1.0]])],"derivedFrom":subQ0}),makeQuery(id+"F36.imprint","IMPRINT",EDGE,{"disambiguationData":[TD([[subQ1,-1.0]])],"derivedFrom":subQ0})])],"isStart":false});}
            chamfer(context, id + "F40", {"entities" : qUnion([Q0, Q1]), "chamferType" : ChamferType.TWO_OFFSETS, "width1" : 0.5 * mm, "oppositeDirection" : false, "width2" : 15 * mm, "tangentPropagation" : true});
        }
    });
